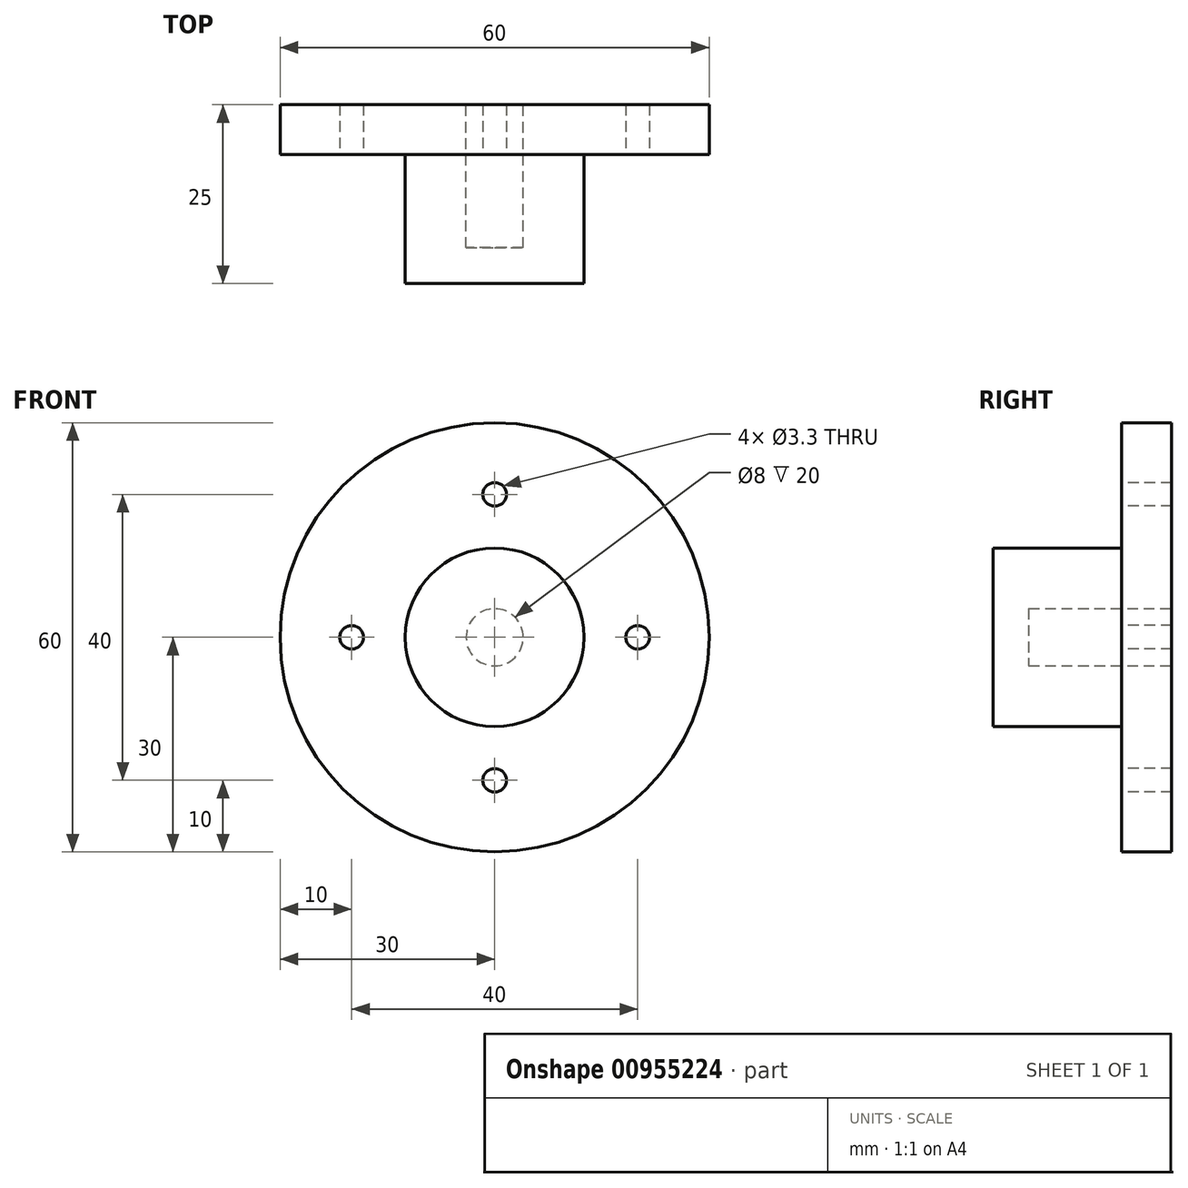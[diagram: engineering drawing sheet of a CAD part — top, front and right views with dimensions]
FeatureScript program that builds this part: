
annotation { "Feature Type Name" : "Feature", "Feature Type Description" : "" }
export const myFeature = defineFeature(function(context is Context, id is Id, definition is map)
    precondition{}
    {
        {
            var Q0;
            Q0=qCreatedBy(makeId("Front.planeOp"),FACE);
            var sketch = newSketch(context, id + "F0", { "sketchPlane" : qUnion([Q0])});
            skCircle(sketch, "E0", {"center": v(0, 0) * mm, "radius": 30 * mm});
            skSolve(sketch);
        }
        {
            var Q0;
            Q0 = qSketchRegion(id + "F0", true);
            extrude(context, id + "F1", {"entities" : qUnion([Q0]), "depth" : 7 * mm, "offsetDistance" : 25 * mm});
        }
        {
            var Q0;
            Q0=makeQuery(id+"F1.opExtrude","CAP_FACE",FACE,{"disambiguationData":[OSD([sQuery(id+"F0.wireOp",EDGE,"E0")])],"isStart":false});
            var sketch = newSketch(context, id + "F2", { "sketchPlane" : qUnion([Q0])});
            skPoint(sketch, "E1", {"position": v(0, 20) * mm});
            skPoint(sketch, "E2.1.0", {"position": v(-20, 0) * mm});
            skPoint(sketch, "E2.2.0", {"position": v(0, -20) * mm});
            skPoint(sketch, "E2.center", {"position": v(0, 0) * mm});
            skPoint(sketch, "E3.0.3.0", {"position": v(20, 0) * mm});
            skSolve(sketch);
        }
        {
            var Q0;
            Q0=sQuery(id+"F2.wireOp",VERTEX,"E1");
            var Q1;
            Q1=sQuery(id+"F2.wireOp",VERTEX,"E3.0.3.0");
            var Q2;
            Q2=sQuery(id+"F2.wireOp",VERTEX,"E2.2.0");
            var Q3;
            Q3=sQuery(id+"F2.wireOp",VERTEX,"E2.1.0");
            var Q4;
            Q4=makeQuery(id+"F1.opExtrude","SWEPT_BODY",BODY,{"disambiguationData":[OSD([sQuery(id+"F0.wireOp",EDGE,"E0")])]});
            hole(context, id + "F3", {"style" : HoleStyle.SIMPLE, "endStyle" : HoleEndStyle.THROUGH, "standardTappedOrClearance" : lookupTablePath({ "standard" : "ISO", "engagement" : "75%", "pitch" : "0.7 mm", "size" : "M4", "type" : "Tapped" }), "standardBlindInLast" : lookupTablePath({ "standard" : "ISO", "fit" : "Normal", "engagement" : "75%", "pitch" : "0.7 mm", "size" : "M4", "type" : "Clearance & tapped" }), "holeDiameter" : 3.3 * mm, "majorDiameter" : 4 * mm, "showTappedDepth" : true, "isTappedThrough" : true, "tappedDepth" : 12 * mm, "tapClearance" : 3, "locations" : qUnion([Q0, Q1, Q2, Q3]), "scope" : qUnion([Q4])});
        }
        {
            var Q0;
            Q0=makeQuery(id+"F1.opExtrude","CAP_FACE",FACE,{"disambiguationData":[OSD([sQuery(id+"F0.wireOp",EDGE,"E0")])],"isStart":false});
            var sketch = newSketch(context, id + "F4", { "sketchPlane" : qUnion([Q0])});
            skCircle(sketch, "E4", {"center": v(0, 0) * mm, "radius": 12.5 * mm});
            skSolve(sketch);
        }
        {
            var Q0;
            Q0 = qSketchRegion(id + "F4", true);
            extrude(context, id + "F5", {"entities" : qUnion([Q0]), "operationType" : NewBodyOperationType.ADD, "depth" : 18 * mm, "offsetDistance" : 25 * mm});
        }
        {
            var Q0;
            Q0=makeQuery(id+"F1.opExtrude","CAP_FACE",FACE,{"disambiguationData":[OSD([sQuery(id+"F0.wireOp",EDGE,"E0")])],"isStart":true});
            var sketch = newSketch(context, id + "F6", { "sketchPlane" : qUnion([Q0])});
            skCircle(sketch, "E5", {"center": v(0, 0) * mm, "radius": 4 * mm});
            skSolve(sketch);
        }
        {
            var Q0;
            Q0 = qSketchRegion(id + "F6", true);
            extrude(context, id + "F7", {"entities" : qUnion([Q0]), "operationType" : NewBodyOperationType.REMOVE, "oppositeDirection" : true, "depth" : 20 * mm, "offsetDistance" : 25 * mm});
        }
        {
            var Q0;
            Q0=qCreatedBy(makeId("Front.planeOp"),FACE);
            var sketch = newSketch(context, id + "F8", { "sketchPlane" : qUnion([Q0])});
            skCircle(sketch, "E6", {"center": v(0, 0) * mm, "radius": 42.26 * mm});
            skSolve(sketch);
        }
        {
            var Q0;
            Q0 = qSketchRegion(id + "F8", true);
            extrude(context, id + "F9", {"entities" : qUnion([Q0]), "depth" : 25 * mm, "offsetDistance" : 25 * mm});
        }
        {
            var Q0;
            Q0=makeQuery(id+"F9.opExtrude","SWEPT_BODY",BODY,{"disambiguationData":[OSD([sQuery(id+"F8.wireOp",EDGE,"E6")])]});
            deleteBodies(context, id + "F10", {"entities" : qUnion([Q0])});
        }
    });
